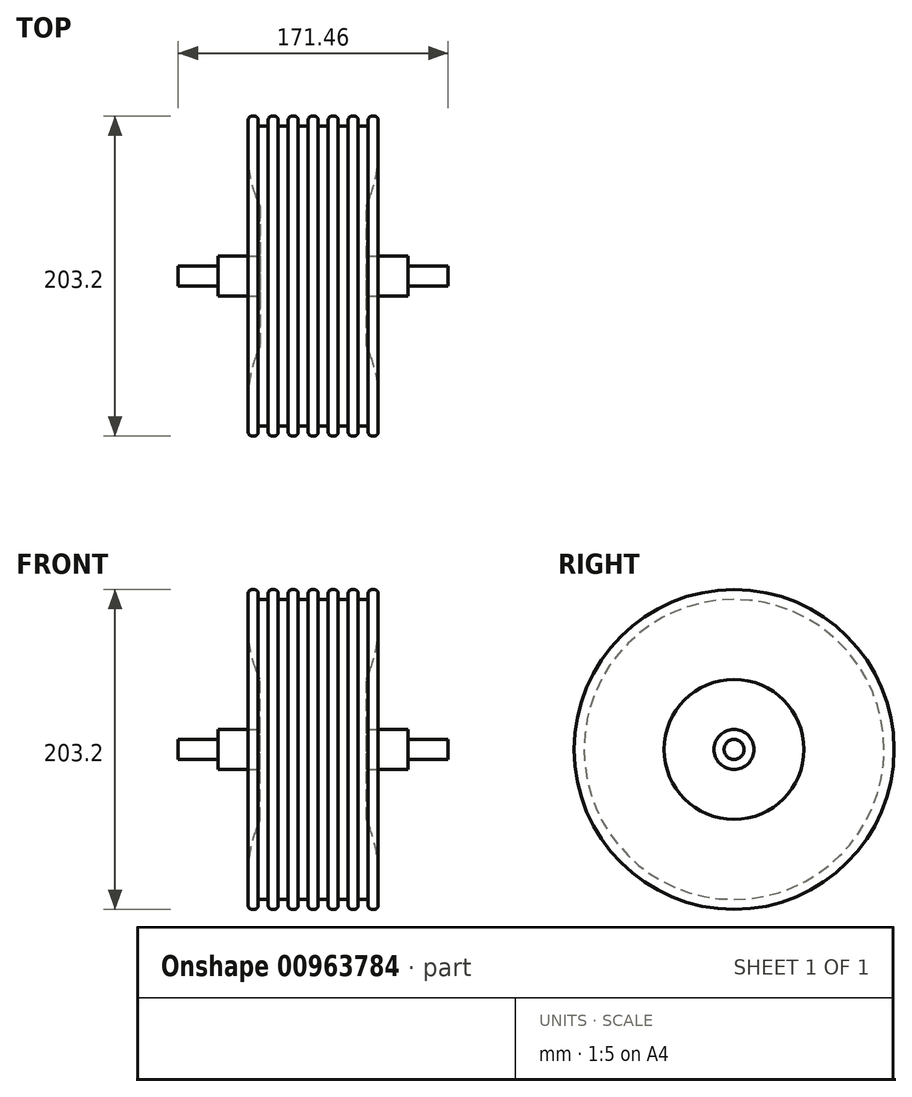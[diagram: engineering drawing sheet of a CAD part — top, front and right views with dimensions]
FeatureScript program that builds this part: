
annotation { "Feature Type Name" : "Feature", "Feature Type Description" : "" }
export const myFeature = defineFeature(function(context is Context, id is Id, definition is map)
    precondition{}
    {
        {
            var Q0;
            Q0=qCreatedBy(makeId("Top.planeOp"),FACE);
            var sketch = newSketch(context, id + "F0", { "sketchPlane" : qUnion([Q0])});
            skLineSegment(sketch, "E0", {"start": v(0, 0) * mm, "end": v(0, 101.6) * mm, "construction": true});
            skLineSegment(sketch, "E1", {"start": v(0, 101.6) * mm, "end": v(3.17, 101.6) * mm});
            skLineSegment(sketch, "E2", {"start": v(3.17, 101.6) * mm, "end": v(3.18, 95.25) * mm});
            skLineSegment(sketch, "E3", {"start": v(3.18, 95.25) * mm, "end": v(9.53, 95.25) * mm});
            skLineSegment(sketch, "E4", {"start": v(9.53, 95.25) * mm, "end": v(9.53, 101.6) * mm});
            skLineSegment(sketch, "E5", {"start": v(9.53, 101.6) * mm, "end": v(15.88, 101.6) * mm});
            skLineSegment(sketch, "E6", {"start": v(15.88, 101.6) * mm, "end": v(15.88, 95.25) * mm});
            skLineSegment(sketch, "E7", {"start": v(15.88, 95.25) * mm, "end": v(22.23, 95.25) * mm});
            skLineSegment(sketch, "E8", {"start": v(22.23, 95.25) * mm, "end": v(22.23, 101.6) * mm});
            skLineSegment(sketch, "E9", {"start": v(41.28, 101.6) * mm, "end": v(41.28, 78.03) * mm});
            skLineSegment(sketch, "E10", {"start": v(36.15, 50.55) * mm, "end": v(33.8, 44.45) * mm});
            skLineSegment(sketch, "E11", {"start": v(33.8, 44.45) * mm, "end": v(33.8, 12.7) * mm});
            skLineSegment(sketch, "E12", {"start": v(60.33, 6.35) * mm, "end": v(85.73, 6.35) * mm});
            skLineSegment(sketch, "E13", {"start": v(85.73, 6.35) * mm, "end": v(85.73, 0) * mm});
            skLineSegment(sketch, "E14", {"start": v(85.73, 0) * mm, "end": v(0, 0) * mm});
            skLineSegment(sketch, "E15", {"start": v(22.23, 101.6) * mm, "end": v(28.58, 101.6) * mm});
            skLineSegment(sketch, "E16", {"start": v(28.58, 101.6) * mm, "end": v(28.58, 95.25) * mm});
            skLineSegment(sketch, "E17", {"start": v(28.58, 95.25) * mm, "end": v(34.93, 95.25) * mm});
            skLineSegment(sketch, "E18", {"start": v(34.93, 95.25) * mm, "end": v(34.93, 101.6) * mm});
            skLineSegment(sketch, "E19", {"start": v(34.93, 101.6) * mm, "end": v(41.28, 101.6) * mm});
            skPoint(sketch, "E20.visualSharp", {"position": v(41.28, 63.8) * mm});
            skArc(sketch, "E20.filletArc", {"start": v(36.15, 50.55) * mm, "mid": v(39.98, 64.05) * mm, "end": v(41.28, 78.03) * mm});
            skLineSegment(sketch, "E21.MirrorCS", {"start": v(-9.53, 101.6) * mm, "end": v(-15.88, 101.6) * mm});
            skLineSegment(sketch, "E22.MirrorCS", {"start": v(-9.53, 95.25) * mm, "end": v(-9.53, 101.6) * mm});
            skLineSegment(sketch, "E23.MirrorCS", {"start": v(-3.18, 95.25) * mm, "end": v(-9.53, 95.25) * mm});
            skLineSegment(sketch, "E24.MirrorCS", {"start": v(-3.17, 101.6) * mm, "end": v(-3.18, 95.25) * mm});
            skLineSegment(sketch, "E25.MirrorCS", {"start": v(0, 101.6) * mm, "end": v(-3.17, 101.6) * mm});
            skLineSegment(sketch, "E26.MirrorCS", {"start": v(-3.18, 101.6) * mm, "end": v(-3.18, 95.25) * mm});
            skLineSegment(sketch, "E27.MirrorCS", {"start": v(-15.88, 101.6) * mm, "end": v(-15.88, 95.25) * mm});
            skLineSegment(sketch, "E28.MirrorCS", {"start": v(-15.88, 95.25) * mm, "end": v(-22.23, 95.25) * mm});
            skLineSegment(sketch, "E29.MirrorCS", {"start": v(-22.23, 95.25) * mm, "end": v(-22.23, 101.6) * mm});
            skLineSegment(sketch, "E30.MirrorCS", {"start": v(-22.23, 101.6) * mm, "end": v(-28.58, 101.6) * mm});
            skLineSegment(sketch, "E31.MirrorCS", {"start": v(-28.58, 101.6) * mm, "end": v(-28.58, 95.25) * mm});
            skLineSegment(sketch, "E32.MirrorCS", {"start": v(-28.58, 95.25) * mm, "end": v(-34.93, 95.25) * mm});
            skLineSegment(sketch, "E33.MirrorCS", {"start": v(-34.93, 95.25) * mm, "end": v(-34.93, 101.6) * mm});
            skLineSegment(sketch, "E34.MirrorCS", {"start": v(-34.93, 101.6) * mm, "end": v(-41.28, 101.6) * mm});
            skLineSegment(sketch, "E35.MirrorCS", {"start": v(-41.28, 101.6) * mm, "end": v(-41.28, 78.03) * mm});
            skArc(sketch, "E36.MirrorCS", {"start": v(-36.15, 50.55) * mm, "mid": v(-39.98, 64.05) * mm, "end": v(-41.28, 78.03) * mm});
            skLineSegment(sketch, "E37.MirrorCS", {"start": v(-36.15, 50.55) * mm, "end": v(-33.8, 44.45) * mm});
            skLineSegment(sketch, "E38.MirrorCS", {"start": v(-33.8, 44.45) * mm, "end": v(-33.8, 12.7) * mm});
            skLineSegment(sketch, "E39.MirrorCS", {"start": v(-60.33, 6.35) * mm, "end": v(-85.73, 6.35) * mm});
            skLineSegment(sketch, "E40.MirrorCS", {"start": v(-85.73, 6.35) * mm, "end": v(-85.73, 0) * mm});
            skLineSegment(sketch, "E41.MirrorCS", {"start": v(-85.73, 0) * mm, "end": v(0, 0) * mm});
            skLineSegment(sketch, "E42", {"start": v(33.8, 12.7) * mm, "end": v(60.33, 12.7) * mm});
            skLineSegment(sketch, "E43", {"start": v(60.33, 12.7) * mm, "end": v(60.33, 6.35) * mm});
            skLineSegment(sketch, "E44.MirrorCS", {"start": v(-33.8, 12.7) * mm, "end": v(-60.33, 12.7) * mm});
            skLineSegment(sketch, "E45.MirrorCS", {"start": v(-60.33, 12.7) * mm, "end": v(-60.33, 6.35) * mm});
            skPoint(sketch, "E46.orphan", {"position": v(33.8, 6.35) * mm});
            skPoint(sketch, "E47.orphan", {"position": v(-33.8, 6.35) * mm});
            skSolve(sketch);
        }
        {
            var Q0;
            Q0=makeQuery(id+"F0.imprint","IMPRINT",FACE,{"disambiguationData":[TD([[makeQuery(id+"F0.imprint","IMPRINT",EDGE,{"derivedFrom":sQuery(id+"F0.wireOp",EDGE,"E1")}),-1.0]])]});
            var Q1;
            Q1=sQuery(id+"F0.wireOp",EDGE,"E14");
            revolve(context, id + "F1", {"surfaceOperationType" : NewSurfaceOperationType.NEW, "entities" : qUnion([Q0]), "axis" : qUnion([Q1]), "revolveType" : RevolveType.FULL});
        }
        {
            var Q0;
            Q0=makeQuery(id+"F1.opRevolve","SWEPT_EDGE",EDGE,{"disambiguationData":[OSD([sQuery(id+"F0.wireOp",EDGE,"E34.MirrorCS"),sQuery(id+"F0.wireOp",EDGE,"E35.MirrorCS")])]});
            var Q1;
            Q1=makeQuery(id+"F1.opRevolve","SWEPT_EDGE",EDGE,{"disambiguationData":[OSD([sQuery(id+"F0.wireOp",EDGE,"E9"),sQuery(id+"F0.wireOp",EDGE,"E19")])]});
            var Q2;
            Q2=makeQuery(id+"F1.opRevolve","SWEPT_EDGE",EDGE,{"disambiguationData":[OSD([sQuery(id+"F0.wireOp",EDGE,"E33.MirrorCS"),sQuery(id+"F0.wireOp",EDGE,"E34.MirrorCS")])]});
            var Q3;
            Q3=makeQuery(id+"F1.opRevolve","SWEPT_EDGE",EDGE,{"disambiguationData":[OSD([sQuery(id+"F0.wireOp",EDGE,"E18"),sQuery(id+"F0.wireOp",EDGE,"E19")])]});
            fillet(context, id + "F2", {"entities" : qUnion([Q0, Q1, Q2, Q3]), "radius" : 2.54 * mm, "tangentPropagation" : true, "allowEdgeOverflow" : false});
        }
        {
            var Q0;
            Q0=makeQuery(id+"F1.opRevolve","SWEPT_EDGE",EDGE,{"disambiguationData":[OSD([sQuery(id+"F0.wireOp",EDGE,"E30.MirrorCS"),sQuery(id+"F0.wireOp",EDGE,"E31.MirrorCS")])]});
            var Q1;
            Q1=makeQuery(id+"F1.opRevolve","SWEPT_EDGE",EDGE,{"disambiguationData":[OSD([sQuery(id+"F0.wireOp",EDGE,"E29.MirrorCS"),sQuery(id+"F0.wireOp",EDGE,"E30.MirrorCS")])]});
            var Q2;
            Q2=makeQuery(id+"F1.opRevolve","SWEPT_EDGE",EDGE,{"disambiguationData":[OSD([sQuery(id+"F0.wireOp",EDGE,"E21.MirrorCS"),sQuery(id+"F0.wireOp",EDGE,"E27.MirrorCS")])]});
            var Q3;
            Q3=makeQuery(id+"F1.opRevolve","SWEPT_EDGE",EDGE,{"disambiguationData":[OSD([sQuery(id+"F0.wireOp",EDGE,"E22.MirrorCS"),sQuery(id+"F0.wireOp",EDGE,"E21.MirrorCS")])]});
            var Q4;
            Q4=makeQuery(id+"F1.opRevolve","SWEPT_EDGE",EDGE,{"disambiguationData":[OSD([sQuery(id+"F0.wireOp",EDGE,"E25.MirrorCS"),sQuery(id+"F0.wireOp",EDGE,"E26.MirrorCS")])]});
            var Q5;
            Q5=makeQuery(id+"F1.opRevolve","SWEPT_EDGE",EDGE,{"disambiguationData":[OSD([sQuery(id+"F0.wireOp",EDGE,"E1"),sQuery(id+"F0.wireOp",EDGE,"E2")])]});
            var Q6;
            Q6=makeQuery(id+"F1.opRevolve","SWEPT_EDGE",EDGE,{"disambiguationData":[OSD([sQuery(id+"F0.wireOp",EDGE,"E4"),sQuery(id+"F0.wireOp",EDGE,"E5")])]});
            var Q7;
            Q7=makeQuery(id+"F1.opRevolve","SWEPT_EDGE",EDGE,{"disambiguationData":[OSD([sQuery(id+"F0.wireOp",EDGE,"E5"),sQuery(id+"F0.wireOp",EDGE,"E6")])]});
            var Q8;
            Q8=makeQuery(id+"F1.opRevolve","SWEPT_EDGE",EDGE,{"disambiguationData":[OSD([sQuery(id+"F0.wireOp",EDGE,"E8"),sQuery(id+"F0.wireOp",EDGE,"E15")])]});
            var Q9;
            Q9=makeQuery(id+"F1.opRevolve","SWEPT_EDGE",EDGE,{"disambiguationData":[OSD([sQuery(id+"F0.wireOp",EDGE,"E15"),sQuery(id+"F0.wireOp",EDGE,"E16")])]});
            fillet(context, id + "F3", {"entities" : qUnion([Q0, Q1, Q2, Q3, Q4, Q5, Q6, Q7, Q8, Q9]), "radius" : 2.54 * mm, "tangentPropagation" : true, "allowEdgeOverflow" : false});
        }
    });
